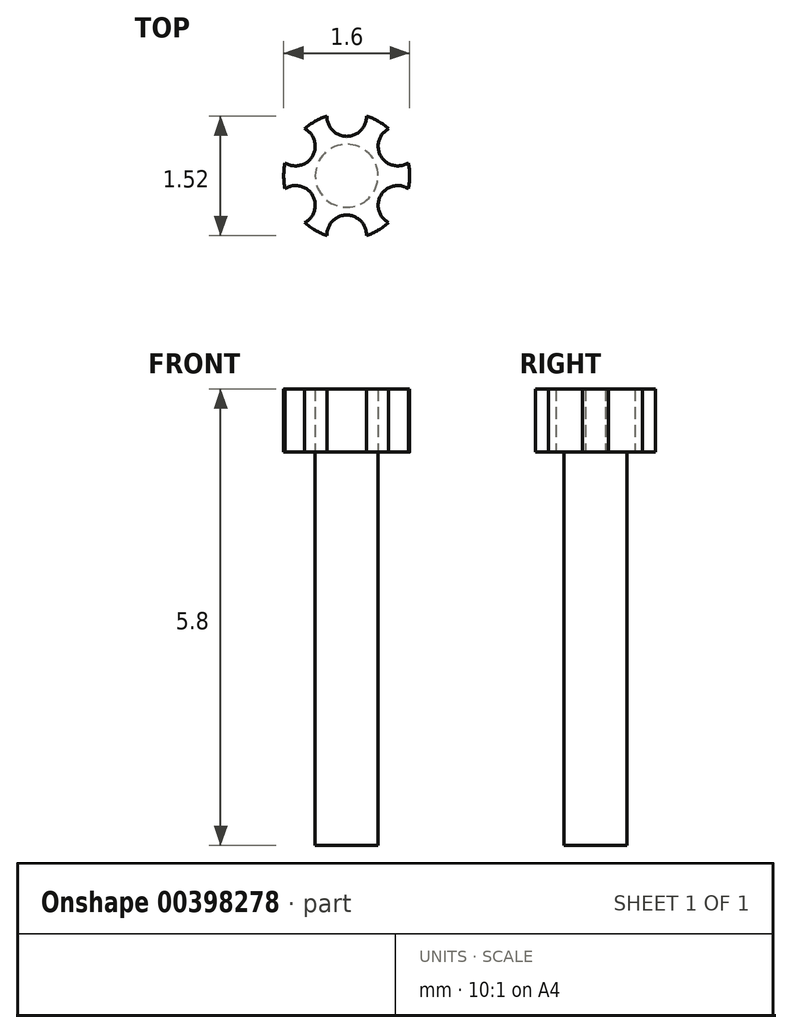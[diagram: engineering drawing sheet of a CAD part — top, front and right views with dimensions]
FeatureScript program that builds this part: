
annotation { "Feature Type Name" : "Feature", "Feature Type Description" : "" }
export const myFeature = defineFeature(function(context is Context, id is Id, definition is map)
    precondition{}
    {
        {
            var Q0;
            Q0=qCreatedBy(makeId("Top.planeOp"),FACE);
            var sketch = newSketch(context, id + "F0", { "sketchPlane" : qUnion([Q0])});
            skCircle(sketch, "E0", {"center": v(0, 0) * mm, "radius": 0.75 * mm, "construction": true});
            skLineSegment(sketch, "E1", {"start": v(0, 0) * mm, "end": v(1.11, 0.64) * mm, "construction": true});
            skLineSegment(sketch, "E2", {"start": v(0, 0) * mm, "end": v(1.05, -0.6) * mm, "construction": true});
            skLineSegment(sketch, "E3", {"start": v(0, 0) * mm, "end": v(-0.96, 0.55) * mm, "construction": true});
            skLineSegment(sketch, "E4", {"start": v(0, 0) * mm, "end": v(-1.02, -0.59) * mm, "construction": true});
            skLineSegment(sketch, "E5", {"start": v(0, 0.75) * mm, "end": v(0, -0.75) * mm, "construction": true});
            skArc(sketch, "E6", {"start": v(-0.25, 0.76) * mm, "mid": v(0, 0.5) * mm, "end": v(0.25, 0.76) * mm});
            skArc(sketch, "E7", {"start": v(0.53, 0.6) * mm, "mid": v(0.43, 0.25) * mm, "end": v(0.78, 0.16) * mm});
            skArc(sketch, "E8", {"start": v(0.78, -0.16) * mm, "mid": v(0.43, -0.25) * mm, "end": v(0.53, -0.6) * mm});
            skArc(sketch, "E9", {"start": v(0.25, -0.76) * mm, "mid": v(0, -0.5) * mm, "end": v(-0.25, -0.76) * mm});
            skArc(sketch, "E10", {"start": v(-0.53, -0.6) * mm, "mid": v(-0.43, -0.25) * mm, "end": v(-0.78, -0.16) * mm});
            skArc(sketch, "E11", {"start": v(-0.78, 0.16) * mm, "mid": v(-0.43, 0.25) * mm, "end": v(-0.53, 0.6) * mm});
            skArc(sketch, "E12", {"start": v(-0.25, 0.76) * mm, "mid": v(-0.4, 0.7) * mm, "end": v(-0.53, 0.6) * mm});
            skArc(sketch, "E13.trimOffspring", {"start": v(0.53, 0.6) * mm, "mid": v(0.4, 0.7) * mm, "end": v(0.25, 0.76) * mm});
            skArc(sketch, "E14.trimOffspring", {"start": v(0.78, -0.16) * mm, "mid": v(0.8, 0) * mm, "end": v(0.78, 0.16) * mm});
            skArc(sketch, "E15.trimOffspring", {"start": v(0.25, -0.76) * mm, "mid": v(0.4, -0.7) * mm, "end": v(0.53, -0.6) * mm});
            skArc(sketch, "E16.trimOffspring", {"start": v(-0.53, -0.6) * mm, "mid": v(-0.4, -0.7) * mm, "end": v(-0.25, -0.76) * mm});
            skArc(sketch, "E17.trimOffspring", {"start": v(-0.78, 0.16) * mm, "mid": v(-0.8, 0) * mm, "end": v(-0.78, -0.16) * mm});
            skSolve(sketch);
        }
        {
            var Q0;
            Q0 = qSketchRegion(id + "F0", true);
            extrude(context, id + "F1", {"entities" : qUnion([Q0]), "depth" : .8 * mm});
        }
        {
            var Q0;
            Q0=qCreatedBy(makeId("Top.planeOp"),FACE);
            var sketch = newSketch(context, id + "F2", { "sketchPlane" : qUnion([Q0])});
            skCircle(sketch, "E18", {"center": v(0, 0) * mm, "radius": 0.4 * mm});
            skSolve(sketch);
        }
        {
            var Q0;
            Q0 = qSketchRegion(id + "F2", true);
            extrude(context, id + "F3", {"entities" : qUnion([Q0]), "operationType" : NewBodyOperationType.ADD, "oppositeDirection" : true, "depth" : 5 * mm});
        }
    });
